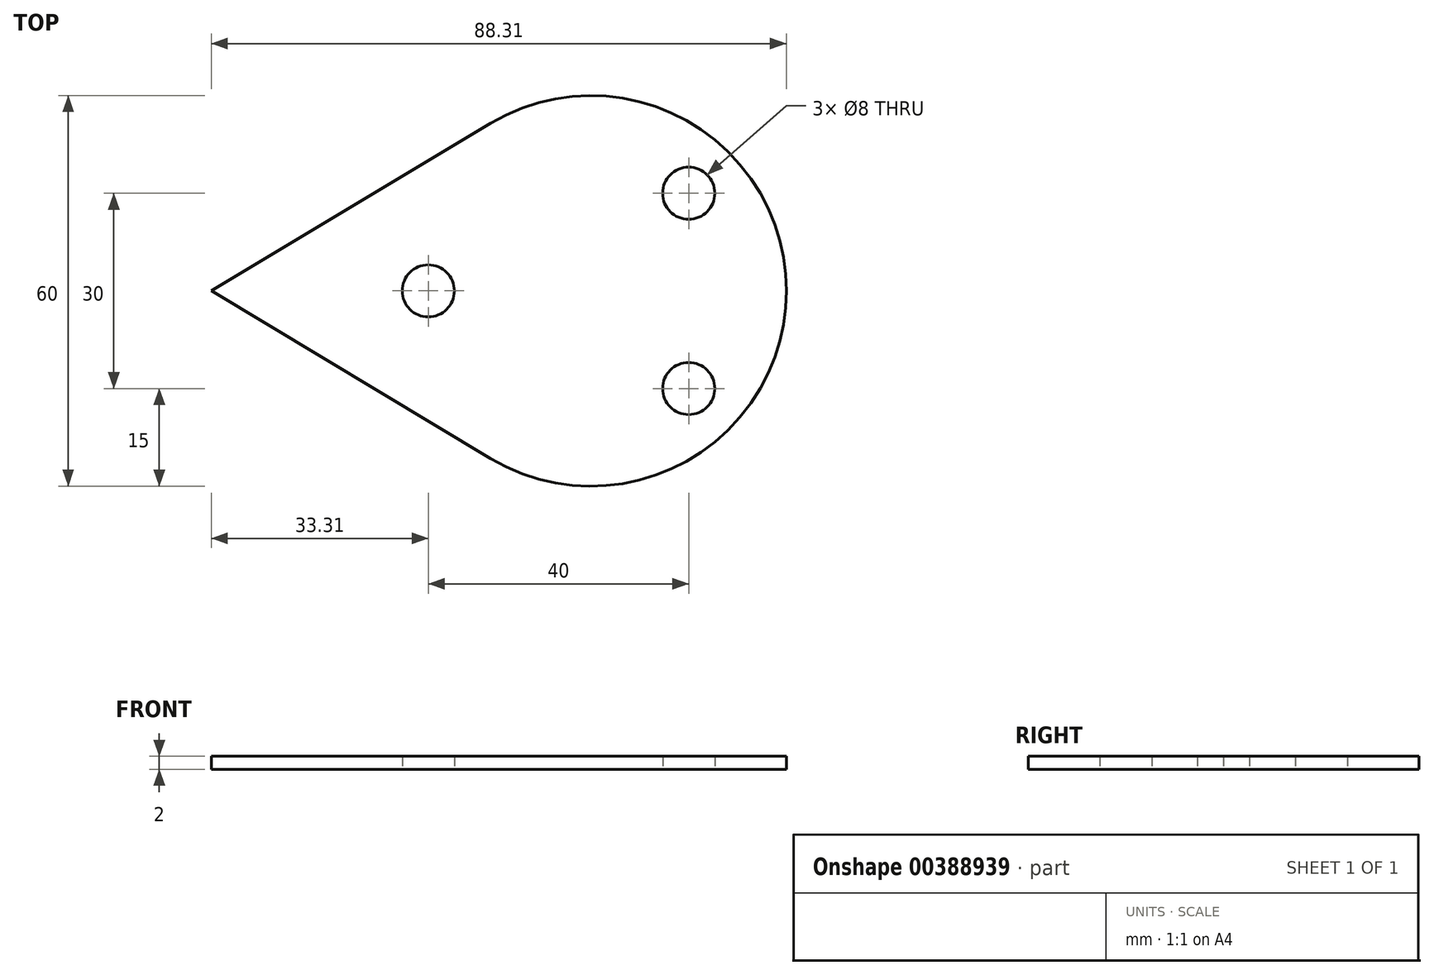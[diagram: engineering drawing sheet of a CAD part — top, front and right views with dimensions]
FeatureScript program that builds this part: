
annotation { "Feature Type Name" : "Feature", "Feature Type Description" : "" }
export const myFeature = defineFeature(function(context is Context, id is Id, definition is map)
    precondition{}
    {
        {
            var Q0;
            Q0=qCreatedBy(makeId("Top.planeOp"),FACE);
            var sketch = newSketch(context, id + "F0", { "sketchPlane" : qUnion([Q0])});
            skLineSegment(sketch, "E0", {"start": v(-58.3, 0) * mm, "end": v(-15.43, 25.72) * mm});
            skArc(sketch, "E1", {"start": v(-15.43, -25.72) * mm, "mid": v(30, 0) * mm, "end": v(-15.43, 25.72) * mm});
            skLineSegment(sketch, "E2", {"start": v(-15.43, -25.72) * mm, "end": v(-58.3, 0) * mm});
            skCircle(sketch, "E3", {"center": v(15, 15) * mm, "radius": 4 * mm});
            skCircle(sketch, "E4", {"center": v(15, -15) * mm, "radius": 4 * mm});
            skCircle(sketch, "E5", {"center": v(-25, 0) * mm, "radius": 4 * mm});
            skLineSegment(sketch, "E6", {"start": v(15, 15) * mm, "end": v(15, -15) * mm, "construction": true});
            skSolve(sketch);
        }
        {
            var Q0;
            Q0=makeQuery(id+"F0.imprint","IMPRINT",FACE,{"disambiguationData":[TD([[makeQuery(id+"F0.imprint","IMPRINT",EDGE,{"derivedFrom":sQuery(id+"F0.wireOp",EDGE,"E0")}),-1.0]])]});
            extrude(context, id + "F1", {"entities" : qUnion([Q0]), "depth" : 2 * mm});
        }
    });
